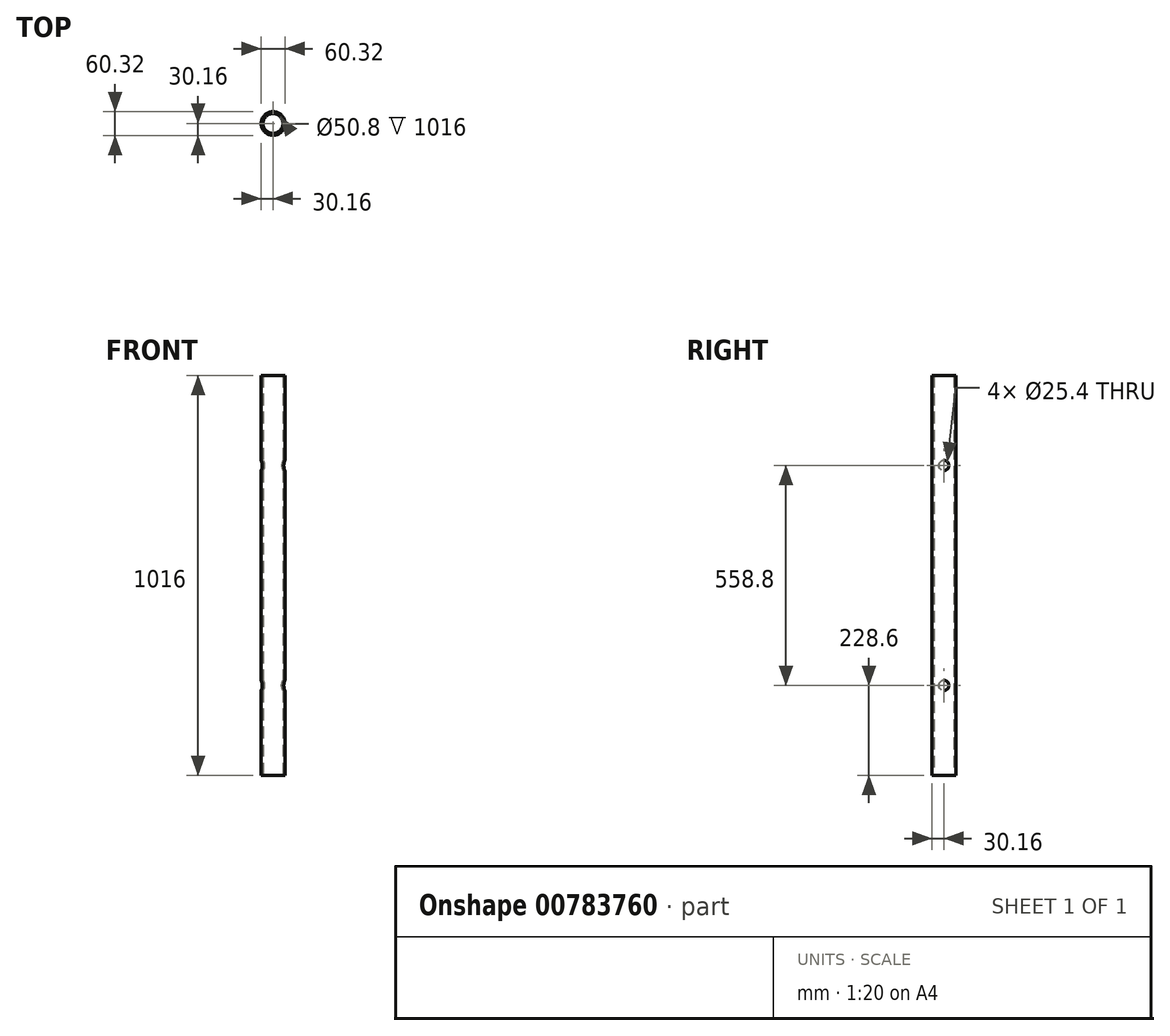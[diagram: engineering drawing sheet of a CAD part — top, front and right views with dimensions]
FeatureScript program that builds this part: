
annotation { "Feature Type Name" : "Feature", "Feature Type Description" : "" }
export const myFeature = defineFeature(function(context is Context, id is Id, definition is map)
    precondition{}
    {
        {
            var Q0;
            Q0=qCreatedBy(makeId("Top.planeOp"),FACE);
            var sketch = newSketch(context, id + "F0", { "sketchPlane" : qUnion([Q0])});
            skCircle(sketch, "E0", {"center": v(0, 0) * mm, "radius": 25.4 * mm});
            skCircle(sketch, "E1", {"center": v(0, 0) * mm, "radius": 30.16 * mm});
            skSolve(sketch);
        }
        {
            var Q0;
            Q0=makeQuery(id+"F0.imprint","IMPRINT",FACE,{"disambiguationData":[TD([[makeQuery(id+"F0.imprint","IMPRINT",EDGE,{"derivedFrom":sQuery(id+"F0.wireOp",EDGE,"E0")}),-1.0]])]});
            extrude(context, id + "F1", {"entities" : qUnion([Q0]), "depth" : 1016 * mm, "offsetDistance" : 25.4 * mm});
        }
        {
            var Q0;
            Q0=qCreatedBy(makeId("Right.planeOp"),FACE);
            var sketch = newSketch(context, id + "F2", { "sketchPlane" : qUnion([Q0])});
            skCircle(sketch, "E2", {"center": v(0, 228.6) * mm, "radius": 12.7 * mm});
            skCircle(sketch, "E3", {"center": v(0, 787.4) * mm, "radius": 12.7 * mm});
            skLineSegment(sketch, "E4", {"start": v(-118.87, 508) * mm, "end": v(136, 508) * mm, "construction": true});
            skSolve(sketch);
        }
        {
            var Q0;
            Q0 = qSketchRegion(id + "F2", true);
            var Q1;
            Q1=makeQuery(id+"F1.opExtrude","SWEPT_FACE",FACE,{"disambiguationData":[OSD([sQuery(id+"F0.wireOp",EDGE,"E1")])]});
            var Q2;
            Q2=makeQuery(id+"F1.opExtrude","SWEPT_FACE",FACE,{"disambiguationData":[OSD([sQuery(id+"F0.wireOp",EDGE,"E1")])]});
            extrude(context, id + "F3", {"entities" : qUnion([Q0]), "operationType" : NewBodyOperationType.REMOVE, "endBound" : BoundingType.UP_TO_SURFACE, "depth" : 25.4 * mm, "endBoundEntityFace" : qUnion([Q1]), "offsetDistance" : 25.4 * mm, "hasSecondDirection" : true, "secondDirectionBound" : SecondDirectionBoundingType.UP_TO_SURFACE, "secondDirectionOppositeDirection" : true, "secondDirectionDepth" : 25.4 * mm, "secondDirectionBoundEntityFace" : qUnion([Q2])});
        }
    });
